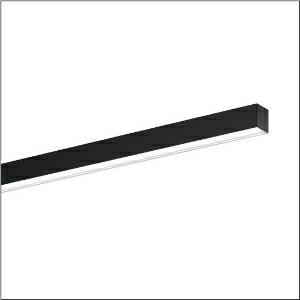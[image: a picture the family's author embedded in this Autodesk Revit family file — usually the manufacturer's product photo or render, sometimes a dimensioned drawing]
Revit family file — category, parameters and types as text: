
# Revit family: silica_r__21_51mx23dc4abb_ae3b
name_source: partatom
category: Lighting Fixtures
units: mm (PartAtom-declared; Revit-internal decimal feet)

## family parameters
Cut with Voids When Loaded = No
Host = Face
Light Source = No
Part Type = Normal
Room Calculation Point = No
Round Connector Dimension = Use Diameter
Shared = No

## types (1)
- --- (1 x LED, 8200 lm, 58.2 W, 4000K)
    Apparent Load = 58 VA
    CIE Flux Codes = 78 96 99 100 100
    Color Rendering = 80
    Color Temperature = 4000K
    Default Elevation = 1800 mm
    Description = Silica® 21, office luminaire, primary optical cover: prismatic diffuser, of PMMA, CAT 2 (L<= 3000cd/m²), light emission: direct distribution, primary light characteristic: symmetric, installation type: surface-mounted, LED, rated luminous flux: 8.200lm, luminous efficacy: 141lm/W, light colour: 840, colour temperature: 4000K, control gear: DALI 2, with terminal, 3+2-pole, max. 2.5mm², mains connection: 220..240V, AC, 50/60Hz, rated input power: 58.2W, luminaire housing, of aluminium, matt jet black (RAL 9005), length: 3.004mm, width: 53mm, height: 53mm, protection rating (complete): IP20, insulation class (complete): insulation class I (protective earthing), certification: CE, permissible operating ambient temperature: 0..+35°C, standard: EN 50419, packaging unit: 1 piece
    Height = 53 mm
    Lamp = 1 x LED
    Lamp Light Flux = 8200 lm
    Lamp Power = 58.2 W
    Lamp count = 1
    Length = 3004 mm
    Luminous efficacy = 141 lm/W
    Manufacturer = Siteco
    ModVariant = No
    Model = 51MX23DC4ABB
    Mounting Place = Ceiling
    Mounting Type = Surface mounted
    Number of Poles = 1
    OnlyDefault = Yes
    Power Factor = 1
    Product Name = Silica® 21
    Product group = office luminaire | ceiling mounted
    ProductGroupID = 302
    Protection Class = Protection class I
    Protection Degree = IP 20
    RLX_Detail_Level = 1
    RLX_Emergency_Light_Flux = 0 lm
    RLX_Emergency_Type = 0
    RLX_Emergency_Type_DB = No
    RlxData = <blob elided: 23717 chars, md5=a09dd897>
    Socket = socket
    Standby Power = 0 W
    System Light Flux = 8200 lm
    System Power = 58 W
    Type Comments = factory setting: luminous flux: 100 % | dim-lin: 254 | 323 mA
    Type Image = l_1335925.jpg
    URL = http://relux.com
    VarID = @adj_119338
    Voltage = 0 V
    Weight = 0.00 kg
    Width = 53 mm

## geometry (parser evidence)
native form markers: Blend x4, Sweep x12
no freeform markers — native parametric forms only
